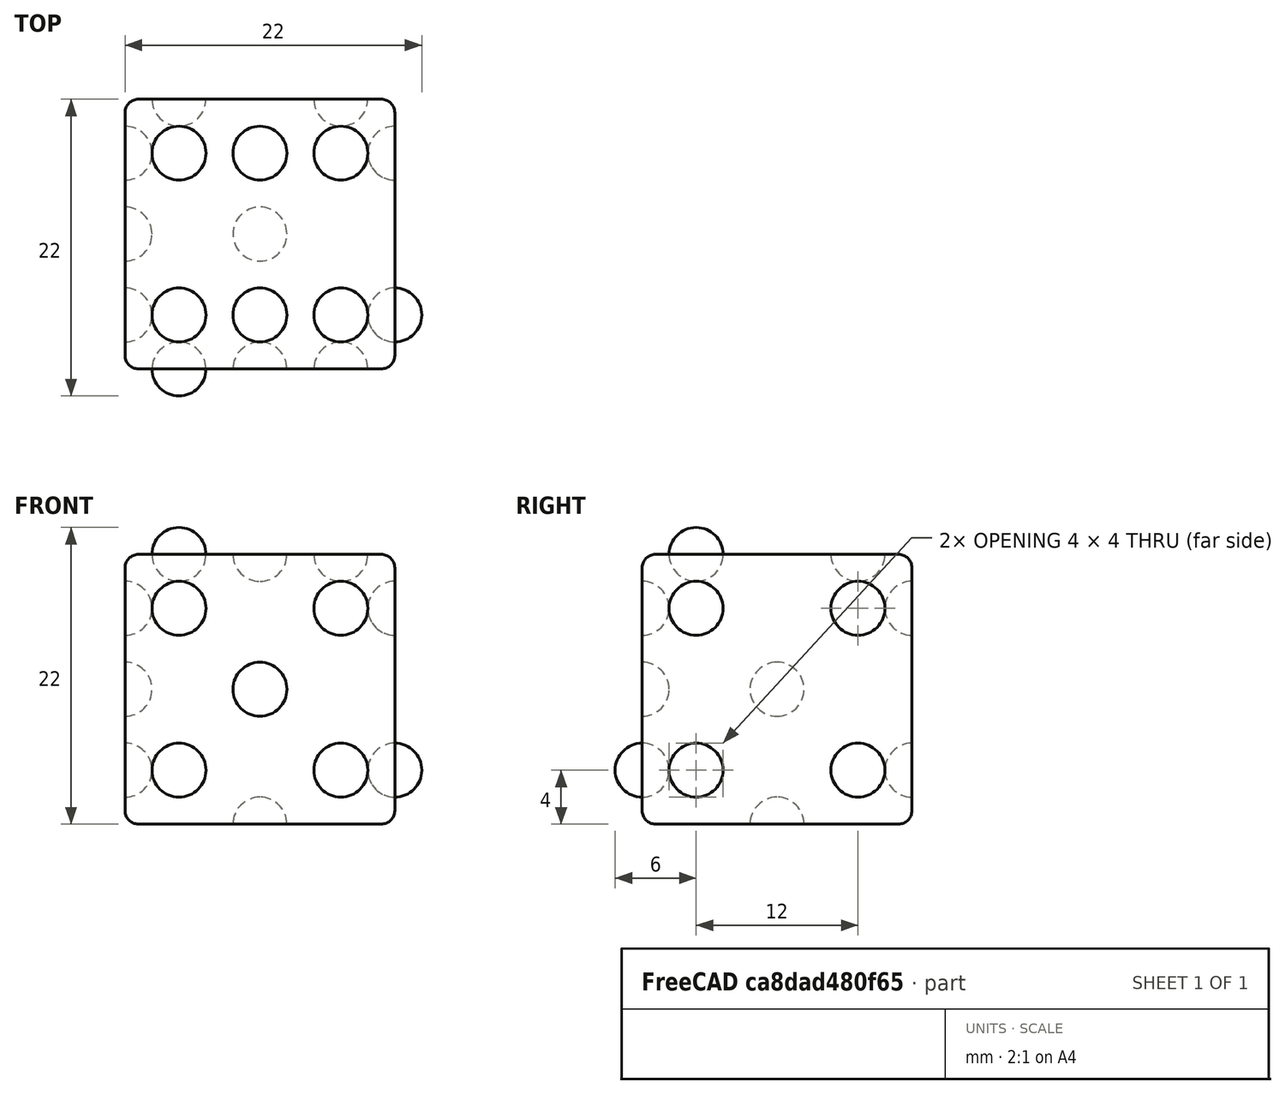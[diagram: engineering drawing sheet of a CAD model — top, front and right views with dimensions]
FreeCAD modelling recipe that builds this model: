
FCSTD DOCUMENT  (FreeCAD 0.21R33694 (Git))
Label: OJT1_T013_Dau
License: All rights reserved
LicenseURL: https://en.wikipedia.org/wiki/All_rights_reserved
objects: Part::Sphere×10, Part::Cut×10, Part::FeaturePython×3, Part::Box×1, Part::Fillet×1
note: 22 computed .brp shape members not serialized (recipe doc carries the construction recipe); baked Part::Feature solids carry a one-line shape summary decoded from their .brp

FEATURE [Part::Box] Box  label="Cub"
  AttacherType = Attacher::AttachEngine3D
  Height = 20
  Length = 20
  Width = 20
FEATURE [Part::Fillet] Fillet
  Base = -> Box
  Edges = 12 edges r=1: [Edge1,Edge2,Edge3,Edge4,Edge5,Edge6,Edge7,Edge8,Edge9,Edge10,Edge11,Edge12]
FEATURE [Part::Sphere] Sphere  label="Esfera"
  Angle1 = -90
  Angle2 = 90
  Angle3 = 360
  AttacherType = Attacher::AttachEngine3D
  Placement = pos=(4,4,20) rot=(0,0,1;0rad)
  Radius = 2
FEATURE [Part::Sphere] Sphere001  label="Esfera001"
  Angle1 = -90
  Angle2 = 90
  Angle3 = 360
  AttacherType = Attacher::AttachEngine3D
  Placement = pos=(4,0,4) rot=(1,0,0;1.5708rad)
  Radius = 2
  expr: .Placement.Rotation.Roll = 90
FEATURE [Part::FeaturePython] Array  # Draft array (typed FeaturePython)
  AlwaysSyncPlacement = false
  Angle = 360
  ArrayType = 0
  Axis = (0,0,1)
  Base = -> Sphere
  Center = (0,0,0)
  Count = 6
  ExpandArray = false
  Fuse = false
  IntervalAxis = (0,0,0)
  IntervalX = (6,0,0)
  IntervalY = (0,12,0)
  IntervalZ = (0,0,100)
  NumberCircles = 3
  NumberPolar = 5
  NumberX = 3
  NumberY = 2
  NumberZ = 1
  PlacementList = 6 placements: [(4,4,20),(4,16,20),(10,4,20),(10,16,20),(16,4,20),(16,16,20)]
  RadialDistance = 50
  ScaleList = (6) [(1,1,1),(1,1,1),(1,1,1),(1,1,1),(1,1,1),(1,1,1)]
  Symmetry = 1
  TangentialDistance = 25
FEATURE [Part::Cut] Cut
  Base = -> Fillet
  Tool = -> Array
FEATURE [Part::FeaturePython] Array001  # Draft array (typed FeaturePython)
  AlwaysSyncPlacement = false
  Angle = 360
  ArrayType = 0
  Axis = (0,0,1)
  Base = -> Sphere001
  Center = (0,0,0)
  Count = 4
  ExpandArray = false
  Fuse = false
  IntervalAxis = (0,0,0)
  IntervalX = (12,0,0)
  IntervalY = (0,0,12)
  IntervalZ = (0,0,100)
  NumberCircles = 3
  NumberPolar = 5
  NumberX = 2
  NumberY = 2
  NumberZ = 1
  PlacementList = 4 placements: [(4,0,4),(4,0,16),(16,0,4),(16,0,16)]
  RadialDistance = 50
  ScaleList = (4) [(1,1,1),(1,1,1),(1,1,1),(1,1,1)]
  Symmetry = 1
  TangentialDistance = 25
FEATURE [Part::Sphere] Sphere002  label="Esfera002"
  Angle1 = -90
  Angle2 = 90
  Angle3 = 360
  AttacherType = Attacher::AttachEngine3D
  Placement = pos=(10,0,10) rot=(1,0,0;1.5708rad)
  Radius = 2
  expr: .Placement.Rotation.Roll = 90
FEATURE [Part::Cut] Cut001
  Base = -> Cut
  Tool = -> Array001
FEATURE [Part::Cut] Cut002
  Base = -> Cut001
  Tool = -> Sphere002
FEATURE [Part::Sphere] Sphere003  label="Esfera003"
  Angle1 = -90
  Angle2 = 90
  Angle3 = 360
  AttacherType = Attacher::AttachEngine3D
  Placement = pos=(20,4,4) rot=(1,0,0;1.5708rad)
  Radius = 2
  expr: .Placement.Rotation.Roll = 90
FEATURE [Part::FeaturePython] Array002  # Draft array (typed FeaturePython)
  AlwaysSyncPlacement = false
  Angle = 360
  ArrayType = 0
  Axis = (0,0,1)
  Base = -> Sphere003
  Center = (0,0,0)
  Count = 4
  ExpandArray = false
  Fuse = false
  IntervalAxis = (0,0,0)
  IntervalX = (0,12,0)
  IntervalY = (0,0,12)
  IntervalZ = (0,0,100)
  NumberCircles = 3
  NumberPolar = 5
  NumberX = 2
  NumberY = 2
  NumberZ = 1
  PlacementList = 4 placements: [(20,4,4),(20,4,16),(20,16,4),(20,16,16)]
  RadialDistance = 50
  ScaleList = (4) [(1,1,1),(1,1,1),(1,1,1),(1,1,1)]
  Symmetry = 1
  TangentialDistance = 25
FEATURE [Part::Cut] Cut003
  Base = -> Cut002
  Tool = -> Array002
FEATURE [Part::Sphere] Sphere004  label="Esfera004"
  Angle1 = -90
  Angle2 = 90
  Angle3 = 360
  AttacherType = Attacher::AttachEngine3D
  Placement = pos=(10,10,0) rot=(0,0,1;0rad)
  Radius = 2
  expr: .Placement.Base.y = 10
FEATURE [Part::Cut] Cut004
  Base = -> Cut003
  Tool = -> Sphere004
FEATURE [Part::Sphere] Sphere005  label="Esfera005"
  Angle1 = -90
  Angle2 = 90
  Angle3 = 360
  AttacherType = Attacher::AttachEngine3D
  Placement = pos=(16,20,4) rot=(0,0,1;0rad)
  Radius = 2
  expr: .Placement.Base.x = 16
  expr: .Placement.Base.y = 20
  expr: .Placement.Base.z = 4
FEATURE [Part::Sphere] Sphere006  label="Esfera006"
  Angle1 = -90
  Angle2 = 90
  Angle3 = 360
  AttacherType = Attacher::AttachEngine3D
  Placement = pos=(4,20,16) rot=(0,0,1;0rad)
  Radius = 2
  expr: .Placement.Base.x = 4
  expr: .Placement.Base.y = 20
  expr: .Placement.Base.z = 16
FEATURE [Part::Cut] Cut005
  Base = -> Cut004
  Tool = -> Sphere005
FEATURE [Part::Cut] Cut006
  Base = -> Cut005
  Tool = -> Sphere006
FEATURE [Part::Sphere] Sphere007  label="Esfera007"
  Angle1 = -90
  Angle2 = 90
  Angle3 = 360
  AttacherType = Attacher::AttachEngine3D
  Placement = pos=(0,10,10) rot=(0,0,1;0rad)
  Radius = 2
  expr: .Placement.Base.x = 0
  expr: .Placement.Base.y = 10
  expr: .Placement.Base.z = 10
FEATURE [Part::Sphere] Sphere008  label="Esfera008"
  Angle1 = -90
  Angle2 = 90
  Angle3 = 360
  AttacherType = Attacher::AttachEngine3D
  Placement = pos=(0,4,4) rot=(0,0,1;0rad)
  Radius = 2
FEATURE [Part::Sphere] Sphere009  label="Esfera009"
  Angle1 = -90
  Angle2 = 90
  Angle3 = 360
  AttacherType = Attacher::AttachEngine3D
  Placement = pos=(0,16,16) rot=(0,0,1;0rad)
  Radius = 2
FEATURE [Part::Cut] Cut007
  Base = -> Cut006
  Tool = -> Sphere007
FEATURE [Part::Cut] Cut008
  Base = -> Cut007
  Tool = -> Sphere008
FEATURE [Part::Cut] Cut009
  Base = -> Cut008
  Tool = -> Sphere009
